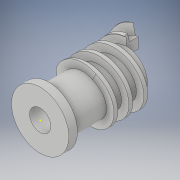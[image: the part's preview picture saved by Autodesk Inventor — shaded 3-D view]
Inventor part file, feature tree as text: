
AUTODESK INVENTOR PART (.ipt)
format: ipt  version: 2018 (Build 220112000, 112)  size: 541,696 bytes
history: native  units: in
note: dims shown in document units (in); Inventor stores cm internally (conversion verified against a paired STEP export)
features: sketch x12, extrude x6, helix x3, other x2, hole x2, plane x1, loft x1, projected_geometry x1
ambient origin geometry x8: Origin, YZ Plane, XZ Plane, XY Plane, X Axis, Y Axis, Z Axis, Center Point
bodies: Solid1 (feature_tree)
feature tree (28):
  sketch  "Sketch1"  dims[d0=2.0in d2=3.9in]
  plane  "Work Plane1"
  sketch  "Sketch2"  dims[d3=0.5in d5=0.0in d6=90.0deg d7=0.0in d8=90.0deg]
  loft  "Loft1"
  other  "Work Point1"
  hole  "Hole1"  [1 undecoded]
  other  "Work Axis2"
  sketch  "Sketch6"  dims[d110=1.0in d111=1.0in d11=0.185in d12=0.75in d13=0.375in d14=0.25in d15=0.5635in d16=1.0in d17=0.8108in d41=0.1in]
  helix  "Coil3"  [1 undecoded]
  helix  "Coil4"  [1 undecoded]
  sketch  "Sketch8"  dims[d42=0.1in d43=0.02in]
  extrude  "Extrusion2"  Depth=0.02in
  helix  "Coil5"  [1 undecoded]
  extrude  "Extrusion3"  Depth=0.1in
  extrude  "Extrusion4"  Depth=0.1in
  sketch  "Sketch12"  dims[d67=0.02in d68=0.1in]
  hole  "Hole2"  [1 undecoded]
  extrude  "Extrusion5"  Depth=0.37in
  extrude  "Extrusion6"  Depth=0.075in
  sketch  "Sketch15"  dims[d72=0.13in d73=1.0in d74=1.5748in d75=0.0in d76=90.0deg d77=90.0deg d78=0.0in d79=0.0in d80=0.37in]
  extrude  "Extrusion7"  TaperAngle=0.0deg  [1 undecoded]
  projected_geometry  "Projected Loop1"
  sketch  "Sketch9"  dims[d44=0.13in d45=1.0in d46=11.811in d47=-0.0739in d48=90.0deg d49=90.0deg d50=0.0in d51=0.0in]
  sketch  "Sketch10"  dims[d52=0.13in d53=1.0in d54=11.811in d55=0.0756in d56=90.0deg d57=90.0deg d58=0.0in d59=0.0in d60=3.775in]
  sketch  "Sketch11"  dims[d63=3.25in d64=0.0in d66=0.1in]
  sketch  "Sketch13"  dims[d69=0.185in d70=0.13in]
  sketch  "Sketch14"  dims[d71=0.5436in]
  sketch  "Sketch16"  dims[d81=0.3in d82=0.0in d83=1.0in d84=0.0in d86=0.02in d87=0.0in d88=0.125in d89=3.0in d90=0.0in d91=0.0in d92=0.5in d108=1.0in d109=1.0in d95=0.185in d96=0.75in d97=0.375in d98=0.25in d99=0.5635in d100=1.0in d101=0.8108in d102=3.4375in d103=0.065in d104=2.87in d105=0.0in d106=2.5in d107=0.0in d112=0.075in d113=0.0in]
note: 6 required parameter values undecoded (feature->parameter linkage not recoverable at this tier; creation-order binding heuristic only, values carry confidence <= 0.55)
